# Revit family: EKF_EE_МонтажнаяПанельГлухаяВысокаяTrivia_AVERES
name_source: partatom
category: Электрооборудование
units: mm (PartAtom-declared; Revit-internal decimal feet)

## family parameters
Всегда вертикально = Нет
На основе рабочей плоскости = Да
Общий = Да
При загрузке вырезать с полостями = Нет
Размер круглого соединителя = Использовать диаметр
Тип детали = Силовой щит
Точка расчета площади = Нет

## types (5) — shared parameters
ADSK_Единица измерения = шт.
ADSK_Завод-изготовитель = EKF
ADSK_Количество = 1
ADSK_Материал = RAL 7035_Сталь
ADSK_Размер_Глубина = 27 мм
Глубина = 400 мм
Изготовитель = EKF
МПГ = Да
Отметка по умолчанию = 1219.2 мм
Серия номенклатуры = Averes
Степень защиты IP = -
ТВ = EKF_2_TRIVIA_AVERES
Тип установки = -
Тип_Панели = Вл_Монтажная панель глухая
zero-valued in all types: ADSK_Масса

## per-type parameters (varying)
| type | ADSK_Код изделия | ADSK_Размер_Высота | ADSK_Размер_Ширина | Тип |
| Монтажная панель В1800 Ш600 глухая EKF AVERES | MP18M600 | 1715 мм | 500 мм | 498 мм |
| Монтажная панель В1800 Ш800 глухая EKF AVERES | MP18M800 | 1715 мм | 700 мм | 500 мм |
| Монтажная панель В2000 Ш400 глухая EKF AVERES | MP20M400 | 1915 мм | 300 мм | 502 мм |
| Монтажная панель В2000 Ш600 глухая EKF AVERES | MP20M600 | 1915 мм | 500 мм | 503 мм |
| Монтажная панель В2000 Ш800 глухая EKF AVERES | MP20M800 | 1915 мм | 700 мм | 505 мм |

note: column(s) folded — value = type name in every type: ADSK_Марка, ADSK_Наименование, ADSK_Обозначение
